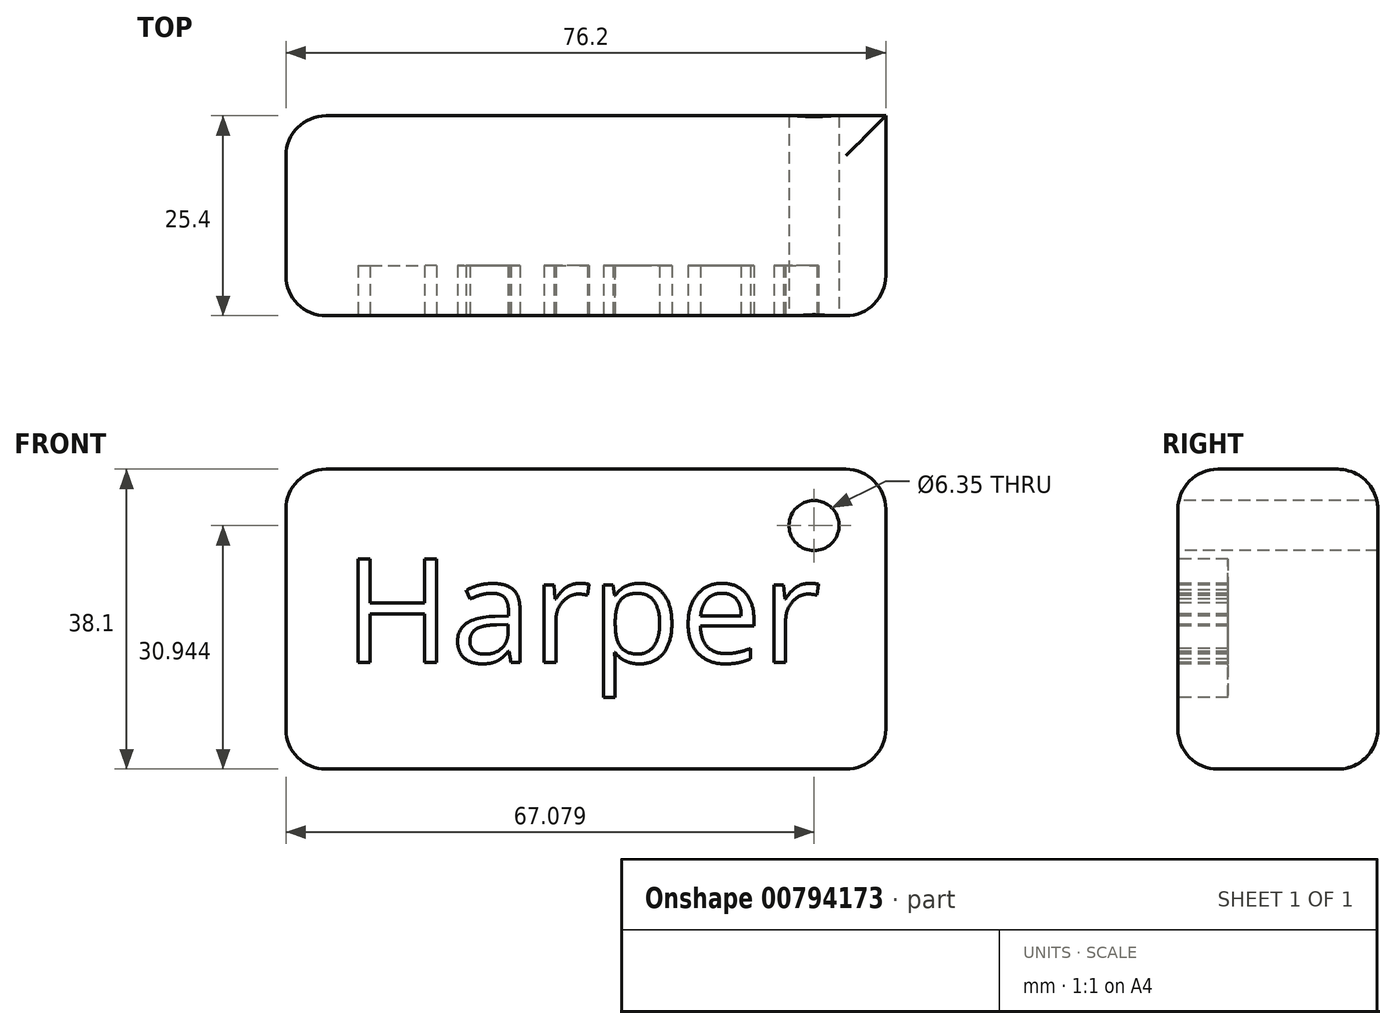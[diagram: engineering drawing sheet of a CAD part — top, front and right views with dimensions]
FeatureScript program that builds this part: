
annotation { "Feature Type Name" : "Feature", "Feature Type Description" : "" }
export const myFeature = defineFeature(function(context is Context, id is Id, definition is map)
    precondition{}
    {
        {
            var Q0;
            Q0=qCreatedBy(makeId("Front.planeOp"),FACE);
            var sketch = newSketch(context, id + "F0", { "sketchPlane" : qUnion([Q0])});
            skLineSegment(sketch, "E0.bottom", {"start": v(-38.1, 19.05) * mm, "end": v(38.1, 19.05) * mm});
            skLineSegment(sketch, "E0.top", {"start": v(-38.1, -19.05) * mm, "end": v(38.1, -19.05) * mm});
            skLineSegment(sketch, "E0.left", {"start": v(-38.1, 19.05) * mm, "end": v(-38.1, -19.05) * mm});
            skLineSegment(sketch, "E0.right", {"start": v(38.1, 19.05) * mm, "end": v(38.1, -19.05) * mm});
            skPoint(sketch, "E0.middle", {"position": v(0, 0) * mm});
            skSolve(sketch);
        }
        {
            var Q0;
            Q0=makeQuery(id+"F0.imprint","IMPRINT",FACE,{"disambiguationData":[TD([[makeQuery(id+"F0.imprint","IMPRINT",EDGE,{"derivedFrom":sQuery(id+"F0.wireOp",EDGE,"E0.bottom")}),-1.0]])]});
            extrude(context, id + "F1", {"entities" : qUnion([Q0]), "depth" : 25.4 * mm, "offsetDistance" : 25.4 * mm});
        }
        {
            var Q0;
            Q0=makeQuery(id+"F1.opExtrude","CAP_FACE",FACE,{"disambiguationData":[OSD([sQuery(id+"F0.wireOp",EDGE,"E0.bottom"),sQuery(id+"F0.wireOp",EDGE,"E0.top"),sQuery(id+"F0.wireOp",EDGE,"E0.left"),sQuery(id+"F0.wireOp",EDGE,"E0.right")])],"isStart":false});
            var sketch = newSketch(context, id + "F2", { "sketchPlane" : qUnion([Q0])});
            skText(sketch, "E1", { "text": "Harper", "fontName": "OpenSans-Regular.ttf"});
            const initialGuessF2  = {"E1": [-0.03075, -0.0055, 1, 0, 0.01328]};
            skSetInitialGuess(sketch, initialGuessF2);
            skSolve(sketch);
        }
        {
            var Q0;
            Q0=makeQuery(id+"F1.opExtrude","CAP_EDGE",EDGE,{"disambiguationData":[OSD([sQuery(id+"F0.wireOp",EDGE,"E0.bottom")])],"isStart":false});
            var Q1;
            Q1=makeQuery(id+"F1.opExtrude","CAP_EDGE",EDGE,{"disambiguationData":[OSD([sQuery(id+"F0.wireOp",EDGE,"E0.right")])],"isStart":false});
            var Q2;
            Q2=makeQuery(id+"F1.opExtrude","SWEPT_EDGE",EDGE,{"disambiguationData":[OSD([sQuery(id+"F0.wireOp",EDGE,"E0.bottom"),sQuery(id+"F0.wireOp",EDGE,"E0.right")])]});
            var Q3;
            Q3=makeQuery(id+"F1.opExtrude","SWEPT_EDGE",EDGE,{"disambiguationData":[OSD([sQuery(id+"F0.wireOp",EDGE,"E0.top"),sQuery(id+"F0.wireOp",EDGE,"E0.right")])]});
            var Q4;
            Q4=makeQuery(id+"F1.opExtrude","CAP_EDGE",EDGE,{"disambiguationData":[OSD([sQuery(id+"F0.wireOp",EDGE,"E0.top")])],"isStart":false});
            var Q5;
            Q5=makeQuery(id+"F1.opExtrude","CAP_EDGE",EDGE,{"disambiguationData":[OSD([sQuery(id+"F0.wireOp",EDGE,"E0.left")])],"isStart":false});
            var Q6;
            Q6=makeQuery(id+"F1.opExtrude","CAP_EDGE",EDGE,{"disambiguationData":[OSD([sQuery(id+"F0.wireOp",EDGE,"E0.left")])],"isStart":true});
            var Q7;
            Q7=makeQuery(id+"F1.opExtrude","SWEPT_EDGE",EDGE,{"disambiguationData":[OSD([sQuery(id+"F0.wireOp",EDGE,"E0.bottom"),sQuery(id+"F0.wireOp",EDGE,"E0.left")])]});
            var Q8;
            Q8=makeQuery(id+"F1.opExtrude","SWEPT_EDGE",EDGE,{"disambiguationData":[OSD([sQuery(id+"F0.wireOp",EDGE,"E0.top"),sQuery(id+"F0.wireOp",EDGE,"E0.left")])]});
            var Q9;
            Q9=makeQuery(id+"F1.opExtrude","CAP_EDGE",EDGE,{"disambiguationData":[OSD([sQuery(id+"F0.wireOp",EDGE,"E0.bottom")])],"isStart":true});
            var Q10;
            Q10=makeQuery(id+"F1.opExtrude","CAP_EDGE",EDGE,{"disambiguationData":[OSD([sQuery(id+"F0.wireOp",EDGE,"E0.top")])],"isStart":true});
            fillet(context, id + "F3", {"entities" : qUnion([Q0, Q1, Q2, Q3, Q4, Q5, Q6, Q7, Q8, Q9, Q10]), "radius" : 5.08 * mm, "tangentPropagation" : true, "allowEdgeOverflow" : false});
        }
        {
            var Q0;
            Q0=makeQuery(id+"F2.imprint","IMPRINT",FACE,{"disambiguationData":[TD([[makeQuery(id+"F2.imprint","IMPRINT",EDGE,{"derivedFrom":sQuery(id+"F2.wireOp",EDGE,"E1.sketch_text.stroke-0")}),1.0]])]});
            var sketch = newSketch(context, id + "F4", { "sketchPlane" : qUnion([Q0])});
            skPoint(sketch, "E2", {"position": v(28.98, 11.9) * mm});
            skSolve(sketch);
        }
        {
            var Q0;
            Q0=sQuery(id+"F4.wireOp",VERTEX,"E2");
            var Q1;
            Q1=makeQuery(id+"F1.opExtrude","SWEPT_BODY",BODY,{"disambiguationData":[OSD([sQuery(id+"F0.wireOp",EDGE,"E0.bottom"),sQuery(id+"F0.wireOp",EDGE,"E0.top"),sQuery(id+"F0.wireOp",EDGE,"E0.left"),sQuery(id+"F0.wireOp",EDGE,"E0.right")])]});
            hole(context, id + "F5", {"style" : HoleStyle.SIMPLE, "endStyle" : HoleEndStyle.THROUGH, "holeDiameter" : 6.35 * mm, "majorDiameter" : 6.35 * mm, "isTappedThrough" : true, "tappedDepth" : 12.7 * mm, "tapClearance" : 3, "locations" : qUnion([Q0]), "scope" : qUnion([Q1])});
        }
        {
            var Q0;
            Q0 = qSketchRegion(id + "F2", true);
            extrude(context, id + "F6", {"entities" : qUnion([Q0]), "operationType" : NewBodyOperationType.REMOVE, "oppositeDirection" : true, "depth" : 6.35 * mm, "offsetDistance" : 25.4 * mm});
        }
    });
